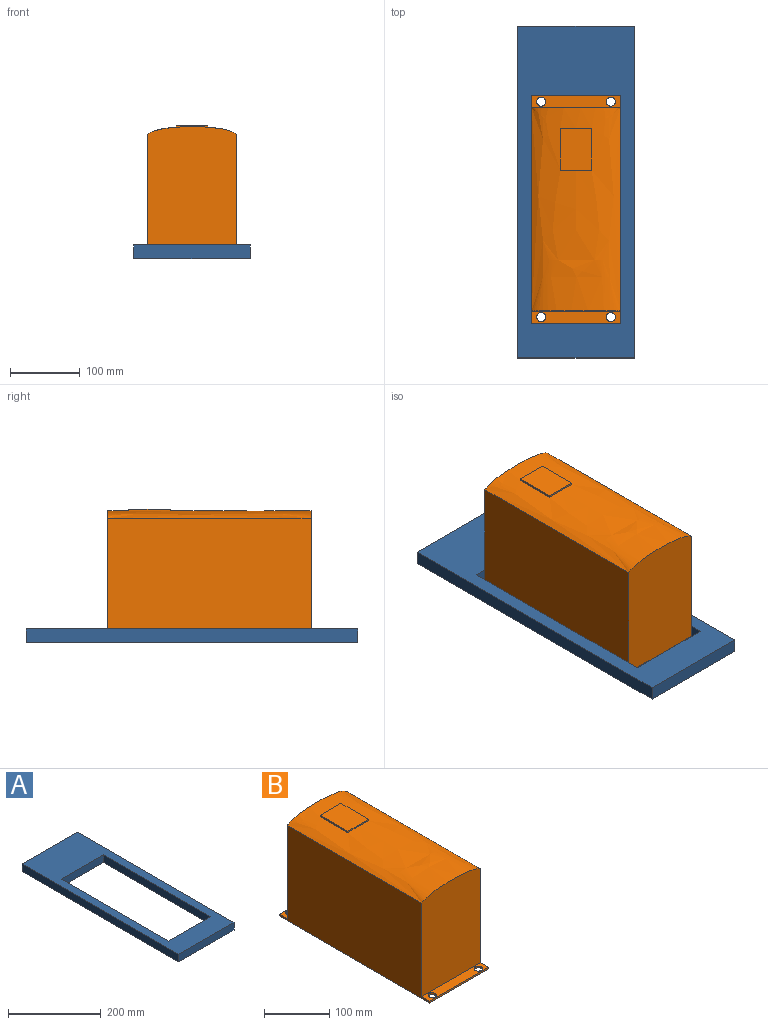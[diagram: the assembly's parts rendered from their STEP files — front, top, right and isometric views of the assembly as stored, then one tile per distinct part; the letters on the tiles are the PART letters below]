
ASSEMBLY  parts=2 mates=1
PART A: 10 faces, bbox 168x477x20 mm
  f0: plane 477x20mm, normal (-1,0,0), area 9540mm2, adj f1,f7,f8,f9
  f1: plane 168x20mm, normal (0,-1,0), area 3360mm2, adj f0,f2,f8,f9
  f2: plane 477x20mm, normal (1,0,0), area 9540mm2, adj f1,f7,f8,f9
  f3: plane 128x20mm, normal (0,1,0), area 2560mm2, adj f4,f6,f8,f9
  f4: plane 327x20mm, normal (1,0,0), area 6540mm2, adj f3,f5,f8,f9
  f5: plane 128x20mm, normal (0,-1,0), area 2560mm2, adj f4,f6,f8,f9
  f6: plane 327x20mm, normal (-1,0,0), area 6540mm2, adj f3,f5,f8,f9
  f7: plane 168x20mm, normal (0,1,0), area 3360mm2, adj f0,f2,f8,f9
  f8: plane 477x168mm, normal (0,0,1), area 38280mm2, adj f0,f1,f2,f3,f4,f5,f6,f7
  f9: plane 477x168mm, normal (0,0,-1), area 38280mm2, adj f0,f1,f2,f3,f4,f5,f6,f7
PART B: 19 faces, bbox 128x327x192 mm
  f0: plane 188.71x128mm, normal (0,-1,0), area 23555.4mm2, adj f1,f2,f12,f13
  f1: plane 327x178.61mm, normal (-1,0,0), area 52265mm2, adj f0,f3,f4,f7,f8,f9,f12,f13
  f2: plane 327x178.61mm, normal (1,0,0), area 52265mm2, adj f0,f3,f4,f7,f8,f9,f12,f13
  f3: plane 188.71x128mm, normal (0,1,0), area 23555.4mm2, adj f1,f2,f8,f13
  f4: plane 327x128mm, normal (0,0,-1), area 41325.1mm2, adj f1,f2,f5,f6,f7,f9,f10,f11
  f5: cylinder r=6.5mm len=13mm, axis (0,0,-1), area 129.7mm2, adj f4,f8
  f6: cylinder r=6.5mm len=13mm, axis (0,0,-1), area 129.7mm2, adj f4,f8
  f7: plane 128x3.18mm, normal (0,1,0), area 406.4mm2, adj f1,f2,f4,f8
  f8: plane 128x17.5mm, normal (0,0,1), area 1974.5mm2, adj f1,f2,f3,f5,f6,f7
  f9: plane 128x3.18mm, normal (0,-1,0), area 406.4mm2, adj f1,f2,f4,f12
  f10: cylinder r=6.5mm len=13mm, axis (0,0,-1), area 129.7mm2, adj f4,f12
  f11: cylinder r=6.5mm len=13mm, axis (0,0,-1), area 129.7mm2, adj f4,f12
  f12: plane 128x17.5mm, normal (0,0,1), area 1974.5mm2, adj f0,f1,f2,f9,f10,f11
  f13: extruded ~292x128mm, area 35777.4mm2, adj f0,f1,f2,f3,f15,f16,f17,f18
  f14: plane 60x45mm, normal (0,0,1), area 2700mm2, adj f15,f16,f17,f18
  f15: plane 45.11x2.82mm, normal (0,1,0), area 101.2mm2, adj f13,f14,f16,f18
  f16: plane 60x2.77mm, normal (1,0,0), area 166.3mm2, adj f13,f14,f15,f17
  f17: plane 45.11x2.82mm, normal (0,-1,0), area 101.2mm2, adj f13,f14,f16,f18
  f18: plane 60x2.77mm, normal (-1,0,0), area 166.3mm2, adj f13,f14,f15,f17
PLACE A at identity
PLACE B at identity
MATE fastened B.f4 <-> A.f9  axis (0,0,-1) through (-64,163.5,0)mm
